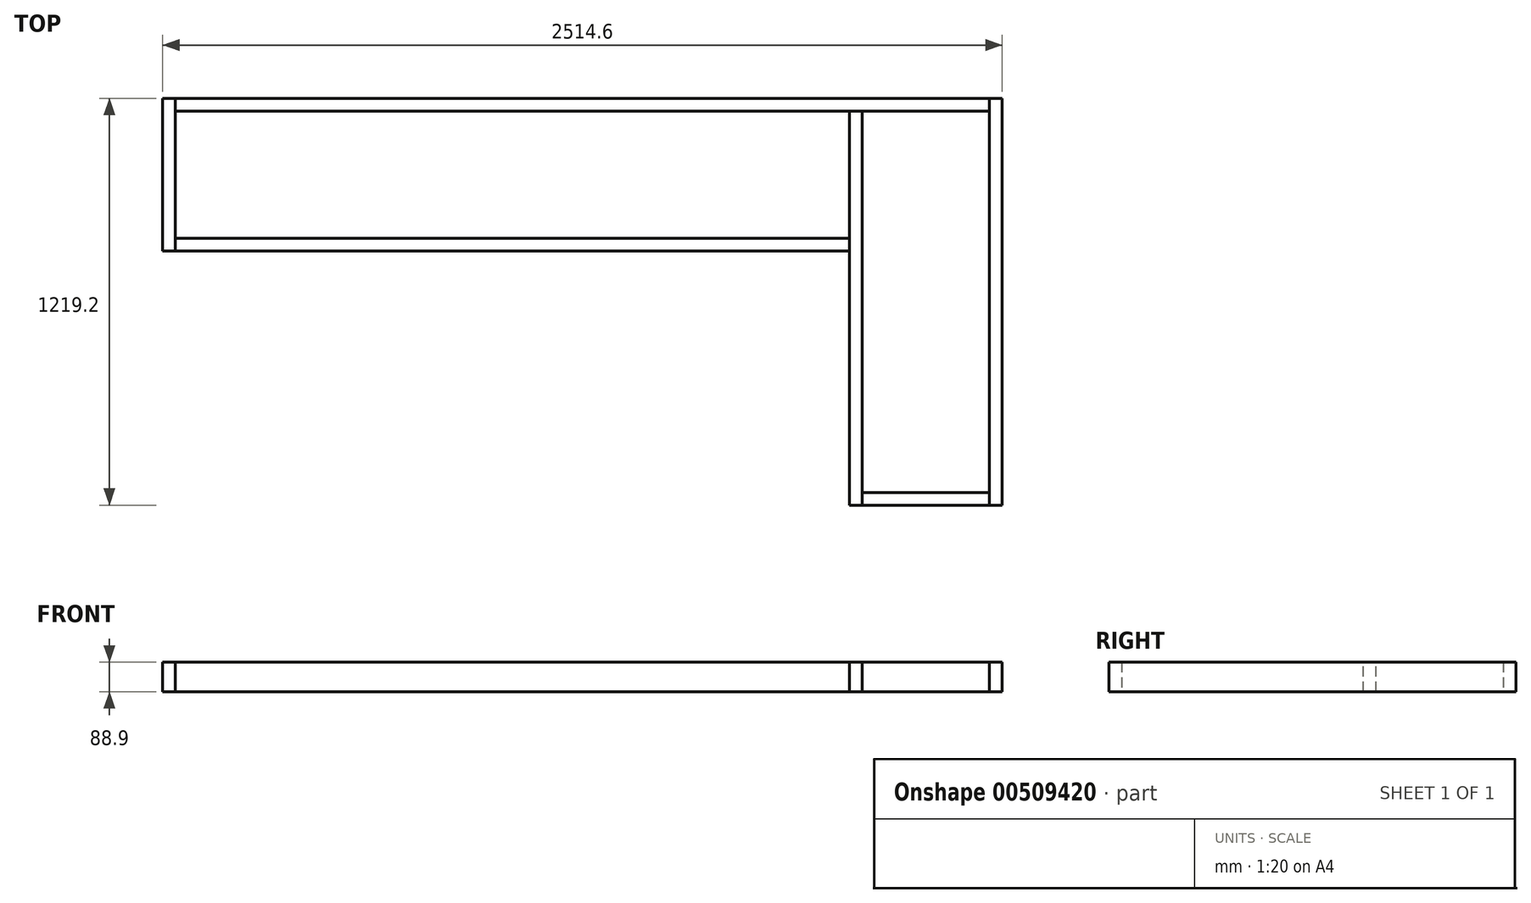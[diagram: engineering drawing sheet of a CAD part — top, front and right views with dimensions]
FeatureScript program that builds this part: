
annotation { "Feature Type Name" : "Feature", "Feature Type Description" : "" }
export const myFeature = defineFeature(function(context is Context, id is Id, definition is map)
    precondition{}
    {
        {
            var Q0;
            Q0=qCreatedBy(makeId("Right.planeOp"),FACE);
            var sketch = newSketch(context, id + "F0", { "sketchPlane" : qUnion([Q0])});
            skLineSegment(sketch, "E0.bottom", {"start": v(0, 0) * mm, "end": v(-38.1, 0) * mm});
            skLineSegment(sketch, "E0.top", {"start": v(0, 88.9) * mm, "end": v(-38.1, 88.9) * mm});
            skLineSegment(sketch, "E0.left", {"start": v(0, 0) * mm, "end": v(0, 88.9) * mm});
            skLineSegment(sketch, "E0.right", {"start": v(-38.1, 0) * mm, "end": v(-38.1, 88.9) * mm});
            skSolve(sketch);
        }
        {
            var Q0;
            Q0 = qSketchRegion(id + "F0", true);
            extrude(context, id + "F1", {"entities" : qUnion([Q0]), "depth" : 2438.4 * mm});
        }
        {
            var Q0;
            Q0=makeQuery(id+"F1.opExtrude","SWEPT_FACE",FACE,{"disambiguationData":[OSD([sQuery(id+"F0.wireOp",EDGE,"E0.right")])]});
            var sketch = newSketch(context, id + "F2", { "sketchPlane" : qUnion([Q0])});
            skLineSegment(sketch, "E1.bottom", {"start": v(-38.1, 0) * mm, "end": v(0, 0) * mm});
            skLineSegment(sketch, "E1.top", {"start": v(-38.1, 88.9) * mm, "end": v(0, 88.9) * mm});
            skLineSegment(sketch, "E1.left", {"start": v(0, 0) * mm, "end": v(0, 88.9) * mm});
            skLineSegment(sketch, "E1.right", {"start": v(-38.1, 0) * mm, "end": v(-38.1, 88.9) * mm});
            skSolve(sketch);
        }
        {
            var Q0;
            Q0 = qSketchRegion(id + "F2", true);
            extrude(context, id + "F3", {"entities" : qUnion([Q0]), "depth" : 419.1 * mm, "hasSecondDirection" : true, "secondDirectionOppositeDirection" : true, "secondDirectionDepth" : 38.1 * mm});
        }
        {
            var Q0;
            Q0=qCreatedBy(makeId("Right.planeOp"),FACE);
            var sketch = newSketch(context, id + "F4", { "sketchPlane" : qUnion([Q0])});
            skLineSegment(sketch, "E2.bottom", {"start": v(-419.1, 0) * mm, "end": v(-457.2, 0) * mm});
            skLineSegment(sketch, "E2.top", {"start": v(-419.1, 88.9) * mm, "end": v(-457.2, 88.9) * mm});
            skLineSegment(sketch, "E2.left", {"start": v(-457.2, 0) * mm, "end": v(-457.2, 88.9) * mm});
            skLineSegment(sketch, "E2.right", {"start": v(-419.1, 0) * mm, "end": v(-419.1, 88.9) * mm});
            skSolve(sketch);
        }
        {
            var Q0;
            Q0 = qSketchRegion(id + "F4", true);
            extrude(context, id + "F5", {"entities" : qUnion([Q0]), "depth" : 2019.3 * mm});
        }
        {
            var Q0;
            Q0=makeQuery(id+"F1.opExtrude","SWEPT_FACE",FACE,{"disambiguationData":[OSD([sQuery(id+"F0.wireOp",EDGE,"E0.right")])]});
            var sketch = newSketch(context, id + "F6", { "sketchPlane" : qUnion([Q0])});
            skLineSegment(sketch, "E3.bottom", {"start": v(2476.5, 0) * mm, "end": v(2438.4, 0) * mm});
            skLineSegment(sketch, "E3.top", {"start": v(2476.5, 88.9) * mm, "end": v(2438.4, 88.9) * mm});
            skLineSegment(sketch, "E3.left", {"start": v(2438.4, 0) * mm, "end": v(2438.4, 88.9) * mm});
            skLineSegment(sketch, "E3.right", {"start": v(2476.5, 0) * mm, "end": v(2476.5, 88.9) * mm});
            skSolve(sketch);
        }
        {
            var Q0;
            Q0 = qSketchRegion(id + "F6", true);
            extrude(context, id + "F7", {"entities" : qUnion([Q0]), "depth" : 1181.1 * mm, "hasSecondDirection" : true, "secondDirectionOppositeDirection" : true, "secondDirectionDepth" : 38.1 * mm});
        }
        {
            var Q0;
            Q0=makeQuery(id+"F7.opExtrude","SWEPT_FACE",FACE,{"disambiguationData":[OSD([sQuery(id+"F6.wireOp",EDGE,"E3.left")])]});
            var sketch = newSketch(context, id + "F8", { "sketchPlane" : qUnion([Q0])});
            skLineSegment(sketch, "E4.bottom", {"start": v(1219.2, 88.9) * mm, "end": v(1181.1, 88.9) * mm});
            skLineSegment(sketch, "E4.top", {"start": v(1219.2, 0) * mm, "end": v(1181.1, 0) * mm});
            skLineSegment(sketch, "E4.left", {"start": v(1219.2, 88.9) * mm, "end": v(1219.2, 0) * mm});
            skLineSegment(sketch, "E4.right", {"start": v(1181.1, 88.9) * mm, "end": v(1181.1, 0) * mm});
            skSolve(sketch);
        }
        {
            var Q0;
            Q0 = qSketchRegion(id + "F8", true);
            extrude(context, id + "F9", {"entities" : qUnion([Q0]), "depth" : 381 * mm});
        }
        {
            var Q0;
            Q0=makeQuery(id+"F9.opExtrude","SWEPT_FACE",FACE,{"disambiguationData":[OSD([sQuery(id+"F8.wireOp",EDGE,"E4.left")])]});
            var sketch = newSketch(context, id + "F10", { "sketchPlane" : qUnion([Q0])});
            skLineSegment(sketch, "E5.bottom", {"start": v(2057.4, 88.9) * mm, "end": v(2019.3, 88.9) * mm});
            skLineSegment(sketch, "E5.top", {"start": v(2057.4, 0) * mm, "end": v(2019.3, 0) * mm});
            skLineSegment(sketch, "E5.left", {"start": v(2057.4, 88.9) * mm, "end": v(2057.4, 0) * mm});
            skLineSegment(sketch, "E5.right", {"start": v(2019.3, 88.9) * mm, "end": v(2019.3, 0) * mm});
            skSolve(sketch);
        }
        {
            var Q0;
            Q0=makeQuery(id+"F10.imprint","IMPRINT",FACE,{"disambiguationData":[TD([[makeQuery(id+"F10.imprint","IMPRINT",EDGE,{"derivedFrom":sQuery(id+"F10.wireOp",EDGE,"E5.bottom")}),1.0]])]});
            var Q1;
            Q1=makeQuery(id+"F1.opExtrude","SWEPT_FACE",FACE,{"disambiguationData":[OSD([sQuery(id+"F0.wireOp",EDGE,"E0.right")])]});
            extrude(context, id + "F11", {"entities" : qUnion([Q0]), "endBound" : BoundingType.UP_TO_SURFACE, "oppositeDirection" : true, "endBoundEntityFace" : qUnion([Q1]), "depth" : 25.4 * mm});
        }
    });
